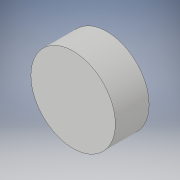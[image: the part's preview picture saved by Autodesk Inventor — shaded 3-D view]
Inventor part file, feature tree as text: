
AUTODESK INVENTOR PART (.ipt)
format: ipt  version: 2018 (Build 220112000, 112)  size: 90,624 bytes
history: native  units: mm
features: extrude x1, sketch x1
ambient origin geometry x8: Origin, YZ Plane, XZ Plane, XY Plane, X Axis, Y Axis, Z Axis, Center Point
bodies: Volumenkörper1 (feature_tree)
feature tree (2):
  extrude  "Extrusion1"  Depth=20.0mm TaperAngle=0.0deg
  sketch  "Skizze1"  dims[d0=50.0mm d1=20.0mm d2=0.0mm]
